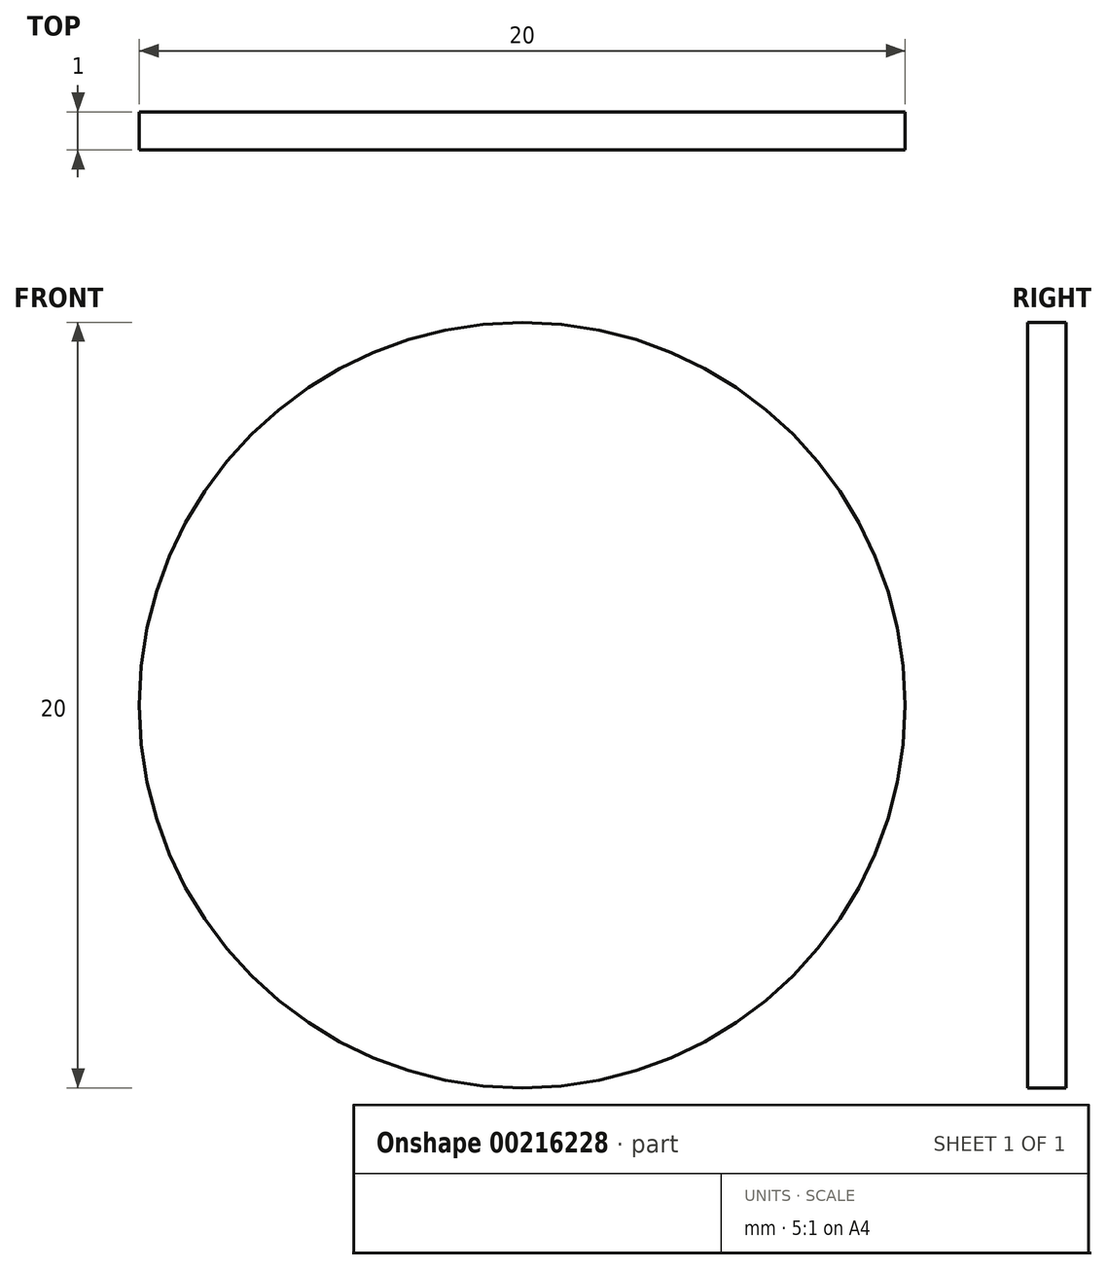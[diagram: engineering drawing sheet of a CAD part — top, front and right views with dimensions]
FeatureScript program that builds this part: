
annotation { "Feature Type Name" : "Feature", "Feature Type Description" : "" }
export const myFeature = defineFeature(function(context is Context, id is Id, definition is map)
    precondition{}
    {
        {
            var Q0;
            Q0=qCreatedBy(makeId("Front.planeOp"),FACE);
            var sketch = newSketch(context, id + "F0", { "sketchPlane" : qUnion([Q0])});
            skCircle(sketch, "E0", {"center": v(0, 0) * mm, "radius": 10 * mm});
            skCircle(sketch, "E1", {"center": v(0, 0) * mm, "radius": 12.5 * mm});
            skSolve(sketch);
        }
        {
            var Q0;
            Q0=makeQuery(id+"F0.imprint","IMPRINT",FACE,{"disambiguationData":[TD([[makeQuery(id+"F0.imprint","IMPRINT",EDGE,{"derivedFrom":sQuery(id+"F0.wireOp",EDGE,"E0")}),1.0]])]});
            extrude(context, id + "F1", {"entities" : qUnion([Q0]), "depth" : 3 * mm});
        }
        {
            var Q0;
            Q0 = qSketchRegion(id + "F0", true);
            var Q1;
            Q1=makeQuery(id+"F1.opExtrude","CAP_FACE",FACE,{"disambiguationData":[OSD([sQuery(id+"F0.wireOp",EDGE,"E0")])],"isStart":false});
            extrude(context, id + "F2", {"entities" : qUnion([Q0, Q1]), "operationType" : NewBodyOperationType.ADD, "depth" : 1 * mm});
        }
        {
            var Q0;
            Q0 = qSketchRegion(id + "F0", true);
            var Q1;
            {var subQ0=sQuery(id+"F0.wireOp",EDGE,"E0");Q1=makeQuery(id+"F2.boolean.opBoolean","MERGE",FACE,{"derivedFrom":[makeQuery(id+"F1.opExtrude","CAP_FACE",FACE,{"disambiguationData":[OSD([subQ0])],"isStart":true}),makeQuery(id+"F2.opExtrude","CAP_FACE",FACE,{"disambiguationData":[OSD([subQ0,sQuery(id+"F0.wireOp",EDGE,"E1")])],"isStart":true})]});}
            extrude(context, id + "F3", {"entities" : qUnion([Q0, Q1]), "operationType" : NewBodyOperationType.REMOVE, "depth" : 3 * mm});
        }
    });
